# Revit family: FU_Table_Sandler_Plania Round_Complete
name_source: partatom
category: Furniture
units: mm (PartAtom-declared; Revit-internal decimal feet)

## family parameters
Always vertical = Yes
Cut with Voids When Loaded = No
OmniClass Number = 23.40.20.00
OmniClass Title = General Furniture and Specialties
Room Calculation Point = No
Shared = No
Work Plane-Based = No

## types (8) — shared parameters
Base Height = 728 mm  [stored 2.38845 ft]
Manufacturer = Sandler
URL = https://www.sandlerseating.com
zero-valued in all types: Default Elevation

## per-type parameters (varying)
| type | Depth | Description | Frame Finish | Height | Leg Finish | Leg Type | Model | Top | Top Thickness | Width |
| Plania 48"/120cm Wood Top - Wooden Legs | 1200 mm  [stored 3.93701 ft] | 120cm / 48″ diameter round table top with standard epoxy painted structural frame. With wooden Legs. | Epoxy - M1_B00 - Black | 750 mm  [stored 2.46063 ft] | Wood - Oak - Walnut | PL30160 | PL50320, PL30160 | PL_Round_Wood : PL50320 - Wood | 22 mm  [stored 0.0721785 ft] | 1200 mm  [stored 3.93701 ft] |
| Plania 55"/140cm Wood Top - Wooden Legs | 1400 mm  [stored 4.59318 ft] | 140cm / 55″ diameter round table top with standard epoxy painted structural frame. With wooden Legs. | Epoxy - M1_B00 - Black | 750 mm  [stored 2.46063 ft] | Wood - Oak - Natural - V | PL30160 | PL50340, PL30160 | PL_Round_Wood : PL50340 - Wood | 22 mm  [stored 0.0721785 ft] | 1400 mm  [stored 4.59318 ft] |
| Plania 48"/120cm HPL/Fenix Top - Wooden Legs | 1200 mm  [stored 3.93701 ft] | 120cm / 48″ diameter round table top with standard epoxy painted structural frame. With wooden Legs. | Epoxy - M1_B00 - Black | 740 mm  [stored 2.42782 ft] | Wood - Oak - Natural - V | PL30160 | PL50320, PL30160 | PL_Round_HPL : PL50320 - HPL/Fenix | 12 mm  [stored 0.0393701 ft] | 1200 mm  [stored 3.93701 ft] |
| Plania 55"/140cm HPL/Fenix Top - Wooden Legs | 1400 mm  [stored 4.59318 ft] | 140cm / 55″ diameter round table top with standard epoxy painted structural frame. With wooden Legs. | Epoxy - M1_B00 - Black | 740 mm  [stored 2.42782 ft] | Wood - Oak - Black - V | PL30160 | PL50340, PL30160 | PL_Round_HPL : PL50340 - HPL/Fenix | 12 mm  [stored 0.0393701 ft] | 1400 mm  [stored 4.59318 ft] |
| Plania 48"/120cm HPL/Fenix Top - Aluminum Legs | 1200 mm  [stored 3.93701 ft] | 120cm / 48″ diameter round table top with standard epoxy painted structural frame. With Aluminum Legs. | Epoxy - M1_B00 - Black | 740 mm  [stored 2.42782 ft] | Epoxy - M1_B00 - Black | PL30060 | PL50320, PL30060 | PL_Round_HPL : PL50320 - HPL/Fenix | 12 mm  [stored 0.0393701 ft] | 1200 mm  [stored 3.93701 ft] |
| Plania 48"/120cm Wood Top - Aluminum Legs | 1200 mm  [stored 3.93701 ft] | 120cm / 48″ diameter round table top with standard epoxy painted structural frame. With aluminum Legs. | Epoxy - M2_G49 | 750 mm  [stored 2.46063 ft] | Epoxy - M2_G49 | PL30060 | PL50320, PL30060 | PL_Round_Wood : PL50320 - Wood | 22 mm  [stored 0.0721785 ft] | 1200 mm  [stored 3.93701 ft] |
| Plania 55"/140cm HPL/Fenix Top - Aluminum Legs | 1400 mm  [stored 4.59318 ft] | 140cm / 55″ diameter round table top with standard epoxy painted structural frame. With aluminum Legs. | Epoxy - M1_Aluminum | 740 mm  [stored 2.42782 ft] | Epoxy - M1_Aluminum | PL30060 | PL50340, PL30060 | PL_Round_HPL : PL50340 - HPL/Fenix | 12 mm  [stored 0.0393701 ft] | 1400 mm  [stored 4.59318 ft] |
| Plania 55"/140cm Wood Top - Aluminum Legs | 1400 mm  [stored 4.59318 ft] | 140cm / 55″ diameter round table top with standard epoxy painted structural frame. With aluminum Legs. | Epoxy - M2 - Rust Brown | 750 mm  [stored 2.46063 ft] | Epoxy - M2 - Rust Brown | PL30060 | PL50340, PL30060 | PL_Round_Wood : PL50340 - Wood | 22 mm  [stored 0.0721785 ft] | 1400 mm  [stored 4.59318 ft] |

note: [stored X ft] marks values corroborated as IEEE doubles in the binary element streams (Revit-internal decimal feet)

## geometry (parser evidence)
native form markers: Sweep x15
no freeform markers — native parametric forms only
